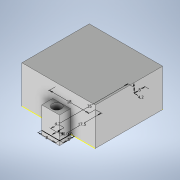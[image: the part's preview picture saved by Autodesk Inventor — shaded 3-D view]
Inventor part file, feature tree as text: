
AUTODESK INVENTOR PART (.ipt)
format: ipt  version: 2020.2 (Build 242310000, 310)  size: 170,496 bytes
history: native  units: in
note: dims shown in document units (in); Inventor stores cm internally (conversion verified against a paired STEP export)
features: extrude x4, sketch x4, projected_geometry x1
ambient origin geometry x8: Origin, YZ Plane, XZ Plane, XY Plane, X Axis, Y Axis, Z Axis, Center Point
bodies: Body1 (feature_tree)
feature tree (9):
  extrude  "Extrusion8"  Depth=1.2008in
  extrude  "Extrusion9"  Depth=0.0394in TaperAngle=0.0deg
  sketch  "Sketch12"  dims[d58=0.0394in d59=0.0394in]
  sketch  "Sketch13"  dims[d60=1.2283in d61=1.122in d62=90.0deg d63=0.6299in d64=0.0in d65=0.7087in d66=0.689in d67=1.378in d68=0.1654in d69=0.1654in d70=0.1575in d71=0.1969in d72=90.0deg d73=0.315in d74=0.1969in d75=0.3937in d76=0.0in d77=0.0787in d78=0.0in]
  extrude  "Extrusion10"  Depth=0.0394in
  extrude  "Extrusion11"  Depth=1.122in
  sketch  "Sketch10"  dims[d53=1.3071in d54=1.2008in]
  sketch  "Sketch11"  dims[d55=90.0deg d56=0.0394in d57=0.0in]
  projected_geometry  "Projected Loop1"
